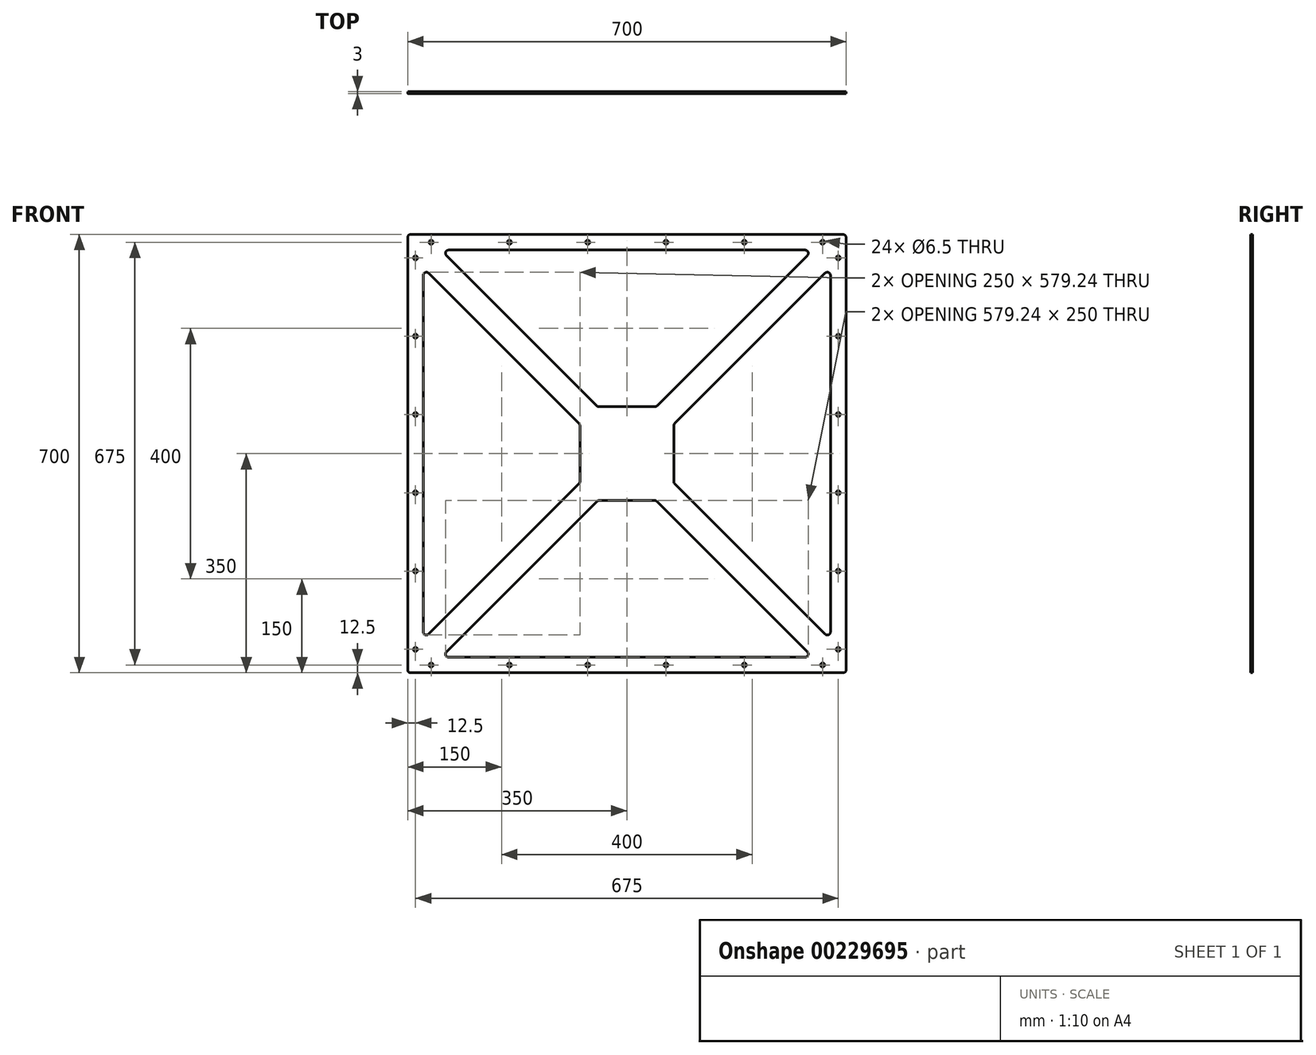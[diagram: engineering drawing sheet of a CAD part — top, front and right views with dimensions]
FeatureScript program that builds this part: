
annotation { "Feature Type Name" : "Feature", "Feature Type Description" : "" }
export const myFeature = defineFeature(function(context is Context, id is Id, definition is map)
    precondition{}
    {
        {
            var Q0;
            Q0=qCreatedBy(makeId("Front.planeOp"),FACE);
            var sketch = newSketch(context, id + "F0", { "sketchPlane" : qUnion([Q0])});
            skLineSegment(sketch, "E0.bottom", {"start": v(345, 350) * mm, "end": v(-345, 350) * mm});
            skLineSegment(sketch, "E0.top", {"start": v(345, -350) * mm, "end": v(-345, -350) * mm});
            skLineSegment(sketch, "E0.left", {"start": v(350, 345) * mm, "end": v(350, -345) * mm});
            skLineSegment(sketch, "E0.right", {"start": v(-350, 345) * mm, "end": v(-350, -345) * mm});
            skPoint(sketch, "E0.middle", {"position": v(0, 0) * mm});
            skLineSegment(sketch, "E1", {"start": v(-350, -350) * mm, "end": v(350, 350) * mm, "construction": true});
            skLineSegment(sketch, "E2", {"start": v(-350, 350) * mm, "end": v(350, -350) * mm, "construction": true});
            skLineSegment(sketch, "E3.0", {"start": v(337.5, 337.5) * mm, "end": v(-337.5, 337.5) * mm, "construction": true});
            skLineSegment(sketch, "E3.1", {"start": v(337.5, 337.5) * mm, "end": v(337.5, -337.5) * mm, "construction": true});
            skLineSegment(sketch, "E3.2", {"start": v(337.5, -337.5) * mm, "end": v(-337.5, -337.5) * mm, "construction": true});
            skLineSegment(sketch, "E3.3", {"start": v(-337.5, 337.5) * mm, "end": v(-337.5, -337.5) * mm, "construction": true});
            skCircle(sketch, "E4", {"center": v(-312.5, 337.5) * mm, "radius": 3.25 * mm});
            skCircle(sketch, "E5.1.0.0", {"center": v(-187.5, 337.5) * mm, "radius": 3.25 * mm});
            skCircle(sketch, "E5.2.0.0", {"center": v(-62.5, 337.5) * mm, "radius": 3.25 * mm});
            skCircle(sketch, "E5.3.0.0", {"center": v(62.5, 337.5) * mm, "radius": 3.25 * mm});
            skCircle(sketch, "E5.4.0.0", {"center": v(187.5, 337.5) * mm, "radius": 3.25 * mm});
            skCircle(sketch, "E5.5.0.0", {"center": v(312.5, 337.5) * mm, "radius": 3.25 * mm});
            skLineSegment(sketch, "E5.direction1", {"start": v(-312.5, 337.5) * mm, "end": v(-187.5, 337.5) * mm, "construction": true});
            skCircle(sketch, "E6.1.1", {"center": v(-337.5, -312.5) * mm, "radius": 3.25 * mm});
            skCircle(sketch, "E6.1.2", {"center": v(-337.5, -187.5) * mm, "radius": 3.25 * mm});
            skCircle(sketch, "E6.1.3", {"center": v(-337.5, -62.5) * mm, "radius": 3.25 * mm});
            skCircle(sketch, "E6.1.4", {"center": v(-337.5, 62.5) * mm, "radius": 3.25 * mm});
            skCircle(sketch, "E6.1.5", {"center": v(-337.5, 187.5) * mm, "radius": 3.25 * mm});
            skCircle(sketch, "E6.1.6", {"center": v(-337.5, 312.5) * mm, "radius": 3.25 * mm});
            skCircle(sketch, "E6.2.1", {"center": v(312.5, -337.5) * mm, "radius": 3.25 * mm});
            skCircle(sketch, "E6.2.2", {"center": v(187.5, -337.5) * mm, "radius": 3.25 * mm});
            skCircle(sketch, "E6.2.3", {"center": v(62.5, -337.5) * mm, "radius": 3.25 * mm});
            skCircle(sketch, "E6.2.4", {"center": v(-62.5, -337.5) * mm, "radius": 3.25 * mm});
            skCircle(sketch, "E6.2.5", {"center": v(-187.5, -337.5) * mm, "radius": 3.25 * mm});
            skCircle(sketch, "E6.2.6", {"center": v(-312.5, -337.5) * mm, "radius": 3.25 * mm});
            skCircle(sketch, "E6.3.1", {"center": v(337.5, 312.5) * mm, "radius": 3.25 * mm});
            skCircle(sketch, "E6.3.2", {"center": v(337.5, 187.5) * mm, "radius": 3.25 * mm});
            skCircle(sketch, "E6.3.3", {"center": v(337.5, 62.5) * mm, "radius": 3.25 * mm});
            skCircle(sketch, "E6.3.4", {"center": v(337.5, -62.5) * mm, "radius": 3.25 * mm});
            skCircle(sketch, "E6.3.5", {"center": v(337.5, -187.5) * mm, "radius": 3.25 * mm});
            skCircle(sketch, "E6.3.6", {"center": v(337.5, -312.5) * mm, "radius": 3.25 * mm});
            skLineSegment(sketch, "E7.right", {"start": v(75, 44.64) * mm, "end": v(75, -44.64) * mm});
            skLineSegment(sketch, "E8.trimOffspring", {"start": v(76.46, -48.18) * mm, "end": v(316.46, -288.18) * mm});
            skLineSegment(sketch, "E9.MirrorCS", {"start": v(316.46, 288.18) * mm, "end": v(76.46, 48.18) * mm});
            skLineSegment(sketch, "E10.trimOffspring", {"start": v(325, 284.64) * mm, "end": v(325, -284.64) * mm});
            skPoint(sketch, "E11.visualSharp", {"position": v(325, 296.72) * mm});
            skArc(sketch, "E11.filletArc", {"start": v(325, 284.64) * mm, "mid": v(321.91, 289.26) * mm, "end": v(316.46, 288.18) * mm});
            skPoint(sketch, "E12.visualSharp", {"position": v(325, -296.72) * mm});
            skArc(sketch, "E12.filletArc", {"start": v(316.46, -288.18) * mm, "mid": v(321.91, -289.26) * mm, "end": v(325, -284.64) * mm});
            skPoint(sketch, "E13.visualSharp", {"position": v(75, -46.72) * mm});
            skArc(sketch, "E13.filletArc", {"start": v(75, -44.64) * mm, "mid": v(75.38, -46.56) * mm, "end": v(76.46, -48.18) * mm});
            skPoint(sketch, "E14.visualSharp", {"position": v(75, 46.72) * mm});
            skArc(sketch, "E14.filletArc", {"start": v(76.46, 48.18) * mm, "mid": v(75.38, 46.56) * mm, "end": v(75, 44.64) * mm});
            skLineSegment(sketch, "E15.1.1", {"start": v(-44.64, 75) * mm, "end": v(44.64, 75) * mm});
            skPoint(sketch, "E15.1.2", {"position": v(-296.72, 325) * mm});
            skLineSegment(sketch, "E15.1.3", {"start": v(48.18, 76.46) * mm, "end": v(288.18, 316.46) * mm});
            skPoint(sketch, "E15.1.4", {"position": v(296.72, 325) * mm});
            skPoint(sketch, "E15.1.5", {"position": v(46.72, 75) * mm});
            skLineSegment(sketch, "E15.1.6", {"start": v(-288.18, 316.46) * mm, "end": v(-48.18, 76.46) * mm});
            skPoint(sketch, "E15.1.7", {"position": v(-46.72, 75) * mm});
            skLineSegment(sketch, "E15.1.8", {"start": v(-284.64, 325) * mm, "end": v(284.64, 325) * mm});
            skArc(sketch, "E15.1.9", {"start": v(-284.64, 325) * mm, "mid": v(-289.26, 321.91) * mm, "end": v(-288.18, 316.46) * mm});
            skArc(sketch, "E15.1.10", {"start": v(288.18, 316.46) * mm, "mid": v(289.26, 321.91) * mm, "end": v(284.64, 325) * mm});
            skArc(sketch, "E15.1.11", {"start": v(-48.18, 76.46) * mm, "mid": v(-46.56, 75.38) * mm, "end": v(-44.64, 75) * mm});
            skArc(sketch, "E15.1.12", {"start": v(44.64, 75) * mm, "mid": v(46.56, 75.38) * mm, "end": v(48.18, 76.46) * mm});
            skLineSegment(sketch, "E15.2.1", {"start": v(-75, -44.64) * mm, "end": v(-75, 44.64) * mm});
            skPoint(sketch, "E15.2.2", {"position": v(-325, -296.72) * mm});
            skLineSegment(sketch, "E15.2.3", {"start": v(-76.46, 48.18) * mm, "end": v(-316.46, 288.18) * mm});
            skPoint(sketch, "E15.2.4", {"position": v(-325, 296.72) * mm});
            skPoint(sketch, "E15.2.5", {"position": v(-75, 46.72) * mm});
            skLineSegment(sketch, "E15.2.6", {"start": v(-316.46, -288.18) * mm, "end": v(-76.46, -48.18) * mm});
            skPoint(sketch, "E15.2.7", {"position": v(-75, -46.72) * mm});
            skLineSegment(sketch, "E15.2.8", {"start": v(-325, -284.64) * mm, "end": v(-325, 284.64) * mm});
            skArc(sketch, "E15.2.9", {"start": v(-325, -284.64) * mm, "mid": v(-321.91, -289.26) * mm, "end": v(-316.46, -288.18) * mm});
            skArc(sketch, "E15.2.10", {"start": v(-316.46, 288.18) * mm, "mid": v(-321.91, 289.26) * mm, "end": v(-325, 284.64) * mm});
            skArc(sketch, "E15.2.11", {"start": v(-76.46, -48.18) * mm, "mid": v(-75.38, -46.56) * mm, "end": v(-75, -44.64) * mm});
            skArc(sketch, "E15.2.12", {"start": v(-75, 44.64) * mm, "mid": v(-75.38, 46.56) * mm, "end": v(-76.46, 48.18) * mm});
            skLineSegment(sketch, "E15.3.1", {"start": v(44.64, -75) * mm, "end": v(-44.64, -75) * mm});
            skPoint(sketch, "E15.3.2", {"position": v(296.72, -325) * mm});
            skLineSegment(sketch, "E15.3.3", {"start": v(-48.18, -76.46) * mm, "end": v(-288.18, -316.46) * mm});
            skPoint(sketch, "E15.3.4", {"position": v(-296.72, -325) * mm});
            skPoint(sketch, "E15.3.5", {"position": v(-46.72, -75) * mm});
            skLineSegment(sketch, "E15.3.6", {"start": v(288.18, -316.46) * mm, "end": v(48.18, -76.46) * mm});
            skPoint(sketch, "E15.3.7", {"position": v(46.72, -75) * mm});
            skLineSegment(sketch, "E15.3.8", {"start": v(284.64, -325) * mm, "end": v(-284.64, -325) * mm});
            skArc(sketch, "E15.3.9", {"start": v(284.64, -325) * mm, "mid": v(289.26, -321.91) * mm, "end": v(288.18, -316.46) * mm});
            skArc(sketch, "E15.3.10", {"start": v(-288.18, -316.46) * mm, "mid": v(-289.26, -321.91) * mm, "end": v(-284.64, -325) * mm});
            skArc(sketch, "E15.3.11", {"start": v(48.18, -76.46) * mm, "mid": v(46.56, -75.38) * mm, "end": v(44.64, -75) * mm});
            skArc(sketch, "E15.3.12", {"start": v(-44.64, -75) * mm, "mid": v(-46.56, -75.38) * mm, "end": v(-48.18, -76.46) * mm});
            skPoint(sketch, "E16.visualSharp", {"position": v(350, 350) * mm});
            skArc(sketch, "E16.filletArc", {"start": v(350, 345) * mm, "mid": v(348.54, 348.54) * mm, "end": v(345, 350) * mm});
            skPoint(sketch, "E17.visualSharp", {"position": v(-350, 350) * mm});
            skArc(sketch, "E17.filletArc", {"start": v(-345, 350) * mm, "mid": v(-348.54, 348.54) * mm, "end": v(-350, 345) * mm});
            skPoint(sketch, "E18.visualSharp", {"position": v(-350, -350) * mm});
            skArc(sketch, "E18.filletArc", {"start": v(-350, -345) * mm, "mid": v(-348.54, -348.54) * mm, "end": v(-345, -350) * mm});
            skPoint(sketch, "E19.visualSharp", {"position": v(350, -350) * mm});
            skArc(sketch, "E19.filletArc", {"start": v(345, -350) * mm, "mid": v(348.54, -348.54) * mm, "end": v(350, -345) * mm});
            skSolve(sketch);
        }
        {
            var Q0;
            Q0 = qSketchRegion(id + "F0", true);
            extrude(context, id + "F1", {"entities" : qUnion([Q0]), "depth" : 3 * mm});
        }
    });
